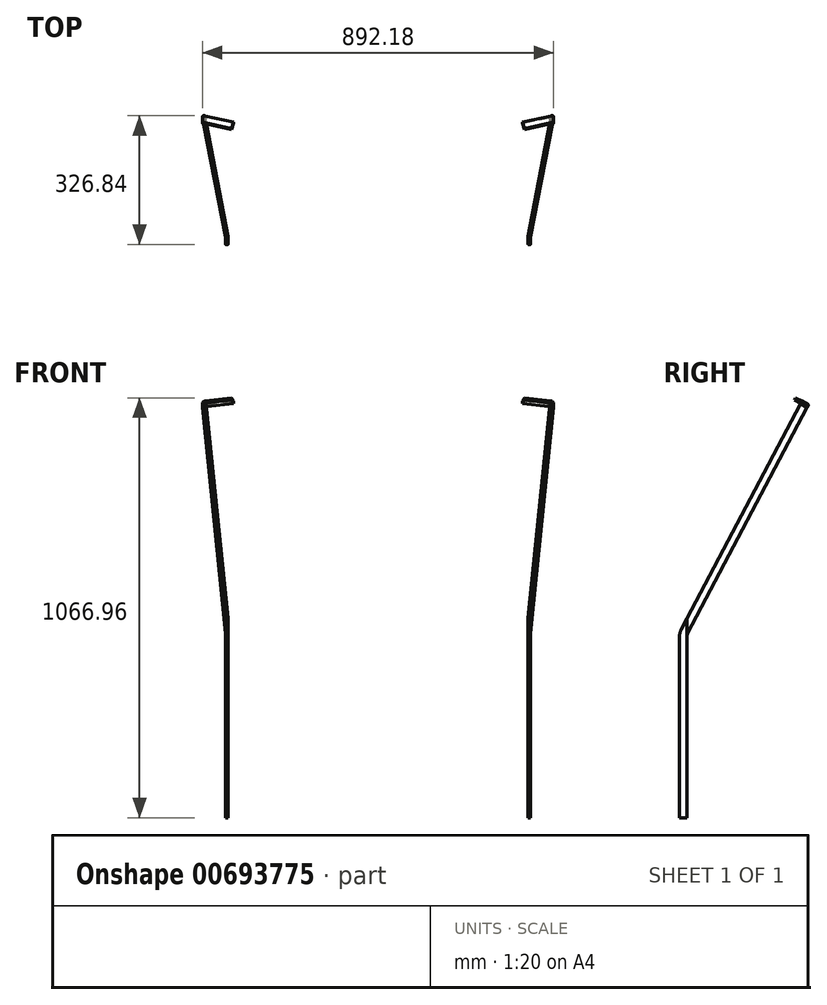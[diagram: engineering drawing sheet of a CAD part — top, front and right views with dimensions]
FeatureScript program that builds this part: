
annotation { "Feature Type Name" : "Feature", "Feature Type Description" : "" }
export const myFeature = defineFeature(function(context is Context, id is Id, definition is map)
    precondition{}
    {
        {
            var Q0;
            Q0=qCreatedBy(makeId("Right.planeOp"),FACE);
            var sketch = newSketch(context, id + "F0", { "sketchPlane" : qUnion([Q0])});
            skLineSegment(sketch, "E0.bottom", {"start": v(0, 0) * mm, "end": v(19.05, 0) * mm});
            skLineSegment(sketch, "E0.left", {"start": v(0, 0) * mm, "end": v(0, 462.04) * mm});
            skLineSegment(sketch, "E0.right", {"start": v(19.05, 0) * mm, "end": v(19.05, 462.04) * mm});
            skLineSegment(sketch, "E1", {"start": v(3.66, 476.85) * mm, "end": v(307.26, 1052.67) * mm});
            skLineSegment(sketch, "E2.0", {"start": v(20.52, 467.97) * mm, "end": v(323.77, 1043.14) * mm});
            skLineSegment(sketch, "E3", {"start": v(307.26, 1052.67) * mm, "end": v(323.77, 1043.14) * mm});
            skPoint(sketch, "E4.visualSharp", {"position": v(19.05, 465.19) * mm});
            skArc(sketch, "E4.filletArc", {"start": v(20.52, 467.97) * mm, "mid": v(19.42, 465.1) * mm, "end": v(19.05, 462.04) * mm});
            skArc(sketch, "E5", {"start": v(3.66, 476.85) * mm, "mid": v(0.93, 469.67) * mm, "end": v(0, 462.04) * mm});
            skPoint(sketch, "E6.orphan", {"position": v(0, 469.9) * mm});
            skLineSegment(sketch, "E7", {"start": v(9.53, 0) * mm, "end": v(9.53, 456.5) * mm, "construction": true});
            skLineSegment(sketch, "E8", {"start": v(315.52, 1047.9) * mm, "end": v(14.75, 477.45) * mm, "construction": true});
            skPoint(sketch, "E9", {"position": v(9.53, 57.15) * mm});
            skPoint(sketch, "E10", {"position": v(9.53, 101.6) * mm});
            skPoint(sketch, "E11", {"position": v(9.53, 127) * mm});
            skPoint(sketch, "E12", {"position": v(9.53, 203.2) * mm});
            skPoint(sketch, "E13", {"position": v(9.53, 355.6) * mm});
            skPoint(sketch, "E14", {"position": v(299.22, 1017) * mm});
            skPoint(sketch, "E15", {"position": v(271.8, 965) * mm});
            skPoint(sketch, "E16", {"position": v(238.46, 901.75) * mm});
            skPoint(sketch, "E17", {"position": v(179.93, 790.74) * mm});
            skPoint(sketch, "E18", {"position": v(149.55, 733.12) * mm});
            skPoint(sketch, "E19", {"position": v(120.65, 678.31) * mm});
            skPoint(sketch, "E20", {"position": v(61.38, 565.89) * mm});
            skPoint(sketch, "E21", {"position": v(29.52, 505.46) * mm});
            skPoint(sketch, "E22", {"position": v(29.73, 505.86) * mm});
            skSolve(sketch);
        }
        {
            var Q0;
            Q0 = qSketchRegion(id + "F0", true);
            extrude(context, id + "F1", {"entities" : qUnion([Q0]), "depth" : 76.2 * mm, "offsetDistance" : 25.4 * mm});
        }
        {
            var Q0;
            Q0=makeQuery(id+"F1.opExtrude","SWEPT_FACE",FACE,{"disambiguationData":[OSD([sQuery(id+"F0.wireOp",EDGE,"E0.left")])]});
            var sketch = newSketch(context, id + "F2", { "sketchPlane" : qUnion([Q0])});
            skLineSegment(sketch, "E23.bottom", {"start": v(6.35, 0) * mm, "end": v(76.2, 0) * mm});
            skLineSegment(sketch, "E23.top", {"start": v(6.35, 462.04) * mm, "end": v(76.2, 462.04) * mm});
            skLineSegment(sketch, "E23.left", {"start": v(6.35, 0) * mm, "end": v(6.35, 462.04) * mm});
            skLineSegment(sketch, "E23.right", {"start": v(76.2, 0) * mm, "end": v(76.2, 462.04) * mm});
            skSolve(sketch);
        }
        {
            var Q0;
            Q0=makeQuery(id+"F1.opExtrude","SWEPT_FACE",FACE,{"disambiguationData":[OSD([sQuery(id+"F0.wireOp",EDGE,"E1")])]});
            cPlane(context, id + "F3", {"entities" : qUnion([Q0]), "cplaneType" : CPlaneType.OFFSET, "offset" : 0 * mm, "width" : 152.4 * mm, "height" : 152.4 * mm});
        }
        {
            var Q0;
            Q0 = qSketchRegion(id + "F2", true);
            extrude(context, id + "F4", {"entities" : qUnion([Q0]), "operationType" : NewBodyOperationType.REMOVE, "endBound" : BoundingType.THROUGH_ALL, "oppositeDirection" : true, "depth" : 25.4 * mm, "offsetDistance" : 25.4 * mm});
        }
        {
            var Q0;
            Q0=qCreatedBy(makeId("Front.planeOp"),FACE);
            var sketch = newSketch(context, id + "F5", { "sketchPlane" : qUnion([Q0])});
            skPoint(sketch, "E24.0", {"position": v(6.35, 462.04) * mm});
            skLineSegment(sketch, "E25", {"start": v(6.9, 467.1) * mm, "end": v(66.3, 1052.67) * mm});
            skLineSegment(sketch, "E26", {"start": v(59.92, 1052.67) * mm, "end": v(0, 462.04) * mm});
            skLineSegment(sketch, "E27.0", {"start": v(66.3, 1052.67) * mm, "end": v(59.92, 1052.67) * mm});
            skPoint(sketch, "E28.orphan", {"position": v(0, 1052.67) * mm});
            skPoint(sketch, "E29.orphan", {"position": v(76.2, 1052.67) * mm});
            skLineSegment(sketch, "E30", {"start": v(0, 462.04) * mm, "end": v(0, 1052.67) * mm});
            skLineSegment(sketch, "E31", {"start": v(0, 1052.67) * mm, "end": v(59.92, 1052.67) * mm});
            skSolve(sketch);
        }
        {
            var Q0;
            Q0=qCreatedBy(makeId("Top.planeOp"),FACE);
            var Q1;
            Q1=sQuery(id+"F5.wireOp",VERTEX,"E28.orphan");
            cPlane(context, id + "F6", {"entities" : qUnion([Q0, Q1]), "cplaneType" : CPlaneType.PLANE_POINT, "offset" : 1059.18 * mm, "width" : 152.4 * mm, "height" : 152.4 * mm});
        }
        {
            var Q0;
            Q0=qCreatedBy(id+"F6.planeOp",FACE);
            var sketch = newSketch(context, id + "F7", { "sketchPlane" : qUnion([Q0])});
            skLineSegment(sketch, "E32.0", {"start": v(6.35, 0) * mm, "end": v(76.2, 0) * mm});
            skLineSegment(sketch, "E33", {"start": v(0, 3.66) * mm, "end": v(0, 19.05) * mm});
            skLineSegment(sketch, "E34.0", {"start": v(6.35, 0) * mm, "end": v(6.35, 19.05) * mm});
            skLineSegment(sketch, "E35", {"start": v(6.35, 19.05) * mm, "end": v(65.06, 323.77) * mm});
            skLineSegment(sketch, "E36.0", {"start": v(0.11, 20.25) * mm, "end": v(58.6, 323.77) * mm});
            skArc(sketch, "E37", {"start": v(0.11, 20.25) * mm, "mid": v(0.03, 19.65) * mm, "end": v(0, 19.05) * mm});
            skLineSegment(sketch, "E38", {"start": v(0.11, 20.25) * mm, "end": v(2.22, 31.18) * mm});
            skLineSegment(sketch, "E39.0", {"start": v(76.2, 323.77) * mm, "end": v(65.06, 323.77) * mm});
            skLineSegment(sketch, "E40.0", {"start": v(0, 307.26) * mm, "end": v(0, 323.77) * mm});
            skLineSegment(sketch, "E41.0", {"start": v(76.2, 307.26) * mm, "end": v(76.2, 323.77) * mm});
            skLineSegment(sketch, "E42.0", {"start": v(0, 19.05) * mm, "end": v(0, 307.26) * mm});
            skLineSegment(sketch, "E43.0", {"start": v(76.2, 0) * mm, "end": v(76.2, 307.26) * mm});
            skPoint(sketch, "E44.orphan", {"position": v(59.92, 0) * mm});
            skPoint(sketch, "E45.orphan", {"position": v(76.2, 3.66) * mm});
            skPoint(sketch, "E46.orphan", {"position": v(0, 3.66) * mm});
            skPoint(sketch, "E47.orphan", {"position": v(0, 0) * mm});
            skLineSegment(sketch, "E48.trimOffspring", {"start": v(58.6, 323.77) * mm, "end": v(0, 323.77) * mm});
            skSolve(sketch);
        }
        {
            var Q0;
            Q0=sQuery(id+"F7.wireOp",EDGE,"E35");
            cPlane(context, id + "F8", {"entities" : qUnion([Q0]), "cplaneType" : CPlaneType.LINE_ANGLE, "offset" : 25.4 * mm, "angle" : 90 * degree, "width" : 152.4 * mm, "height" : 152.4 * mm});
        }
        {
            var Q0;
            Q0=makeQuery(id+"F7.imprint","IMPRINT",FACE,{"disambiguationData":[TD([[makeQuery(id+"F7.imprint","IMPRINT",EDGE,{"derivedFrom":sQuery(id+"F7.wireOp",EDGE,"E36.0")}),1.0]])]});
            var Q1;
            Q1=makeQuery(id+"F7.imprint","IMPRINT",FACE,{"disambiguationData":[TD([[makeQuery(id+"F7.imprint","IMPRINT",EDGE,{"derivedFrom":sQuery(id+"F7.wireOp",EDGE,"E32.0")}),1.0]])]});
            extrude(context, id + "F9", {"entities" : qUnion([Q0, Q1]), "operationType" : NewBodyOperationType.REMOVE, "endBound" : BoundingType.THROUGH_ALL, "oppositeDirection" : true, "depth" : 25.4 * mm, "offsetDistance" : 25.4 * mm});
        }
        {
            var Q0;
            Q0=qCreatedBy(id+"F8.planeOp",FACE);
            var sketch = newSketch(context, id + "F10", { "sketchPlane" : qUnion([Q0])});
            skLineSegment(sketch, "E49.0", {"start": v(19.9, 506.03) * mm, "end": v(313.42, 1052.67) * mm});
            skLineSegment(sketch, "E50.0", {"start": v(21.4, 467.97) * mm, "end": v(330.23, 1043.14) * mm});
            skSolve(sketch);
        }
        {
            var Q0;
            Q0=qCreatedBy(id+"F3.planeOp",FACE);
            var sketch = newSketch(context, id + "F11", { "sketchPlane" : qUnion([Q0])});
            skPoint(sketch, "E51.0", {"position": v(55.42, 1074.48) * mm});
            skLineSegment(sketch, "E52", {"start": v(-51.16, 1074.73) * mm, "end": v(-51.16, 1081.08) * mm});
            skLineSegment(sketch, "E53", {"start": v(-51.16, 1081.08) * mm, "end": v(58.57, 1080.82) * mm});
            skLineSegment(sketch, "E54.0", {"start": v(53.7, 1074.48) * mm, "end": v(-51.16, 1074.73) * mm});
            skArc(sketch, "E55.filletArc", {"start": v(55.28, 1073.02) * mm, "mid": v(54.78, 1074.06) * mm, "end": v(53.7, 1074.48) * mm});
            skPoint(sketch, "E56.orphan", {"position": v(61.88, 1074.48) * mm});
            skPoint(sketch, "E57.0.start.orphan", {"position": v(6.35, 456.51) * mm});
            skPoint(sketch, "E58.0.start.orphan", {"position": v(0.11, 459.09) * mm});
            skLineSegment(sketch, "E59.0", {"start": v(65, 1073) * mm, "end": v(65.06, 1073.75) * mm});
            skLineSegment(sketch, "E60.0.0", {"start": v(6.35, 423.52) * mm, "end": v(6.35, 456.51) * mm});
            skEllipticalArc(sketch, "E60.0.4", {});
            skLineSegment(sketch, "E60.0.5", {"start": v(0, 456.51) * mm, "end": v(0, 423.52) * mm});
            skLineSegment(sketch, "E60.0.6", {"start": v(0, 423.52) * mm, "end": v(6.35, 423.52) * mm});
            skLineSegment(sketch, "E61", {"start": v(55.28, 1073.02) * mm, "end": v(65, 1073) * mm});
            skArc(sketch, "E62", {"start": v(65.06, 1073.75) * mm, "mid": v(63.37, 1078.7) * mm, "end": v(58.57, 1080.82) * mm});
            skPoint(sketch, "E63.orphan", {"position": v(6.63, 423.52) * mm});
            const initialGuessF11  = {"E60.0.4": [0.00635, 0.45651053869236363, 0, 1, 0.013615310578773647, 0.00634999895801842, 1.3804491440357622, 1.5707963267948966]};
            skSetInitialGuess(sketch, initialGuessF11);
            skSolve(sketch);
        }
        {
            var Q0;
            Q0=makeQuery(id+"F11.imprint","IMPRINT",FACE,{"disambiguationData":[TD([[makeQuery(id+"F11.imprint","IMPRINT",EDGE,{"derivedFrom":sQuery(id+"F11.wireOp",EDGE,"E52")}),-1.0]])]});
            extrude(context, id + "F12", {"entities" : qUnion([Q0]), "operationType" : NewBodyOperationType.ADD, "endBound" : BoundingType.SYMMETRIC, "depth" : 76.2 * mm, "offsetDistance" : 25.4 * mm});
        }
        {
            var Q0;
            Q0=makeQuery(id+"F12.opExtrude","SWEPT_FACE",FACE,{"disambiguationData":[OSD([sQuery(id+"F11.wireOp",EDGE,"E53")])]});
            var sketch = newSketch(context, id + "F13", { "sketchPlane" : qUnion([Q0])});
            skLineSegment(sketch, "E64.0", {"start": v(60.17, -199.7) * mm, "end": v(57.2, -217.64) * mm});
            skLineSegment(sketch, "E65", {"start": v(63.46, -199.36) * mm, "end": v(61.5, -199.36) * mm});
            skLineSegment(sketch, "E66", {"start": v(63.44, -218.52) * mm, "end": v(-11.78, -237.46) * mm});
            skLineSegment(sketch, "E67.0", {"start": v(61.5, -199.36) * mm, "end": v(-16.43, -218.99) * mm});
            skLineSegment(sketch, "E68", {"start": v(-16.43, -218.99) * mm, "end": v(-11.78, -237.46) * mm});
            skPoint(sketch, "E69.orphan", {"position": v(60.22, -199.36) * mm});
            skLineSegment(sketch, "E70.0", {"start": v(-53.7, -257.26) * mm, "end": v(-53.7, -257.26) * mm});
            skLineSegment(sketch, "E71", {"start": v(63.46, -181.06) * mm, "end": v(63.46, -199.36) * mm});
            skLineSegment(sketch, "E72.0", {"start": v(63.46, -181.06) * mm, "end": v(50.64, -181.06) * mm});
            skLineSegment(sketch, "E73.0", {"start": v(-53.7, -181.06) * mm, "end": v(50.64, -181.06) * mm});
            skLineSegment(sketch, "E74.0", {"start": v(-53.7, -257.26) * mm, "end": v(-53.7, -181.06) * mm});
            skLineSegment(sketch, "E75.0", {"start": v(63.44, -257.26) * mm, "end": v(-53.7, -257.26) * mm});
            skLineSegment(sketch, "E76.0", {"start": v(63.44, -257.26) * mm, "end": v(63.44, -218.52) * mm});
            skLineSegment(sketch, "E77.trimOffspring", {"start": v(63.44, -199.36) * mm, "end": v(63.44, -181.06) * mm});
            skSolve(sketch);
        }
        {
            var Q0;
            Q0 = qSketchRegion(id + "F13", true);
            extrude(context, id + "F14", {"entities" : qUnion([Q0]), "operationType" : NewBodyOperationType.REMOVE, "oppositeDirection" : true, "depth" : 7.94 * mm, "offsetDistance" : 25.4 * mm});
        }
        {
            var Q0;
            Q0=qCreatedBy(makeId("Right.planeOp"),FACE);
            cPlane(context, id + "F15", {"entities" : qUnion([Q0]), "cplaneType" : CPlaneType.OFFSET, "offset" : 381 * mm, "oppositeDirection" : true, "width" : 152.4 * mm, "height" : 152.4 * mm});
        }
        {
            var Q0;
            Q0=makeQuery(id+"F1.opExtrude","SWEPT_BODY",BODY,{"disambiguationData":[OSD([sQuery(id+"F0.wireOp",EDGE,"E0.bottom"),sQuery(id+"F0.wireOp",EDGE,"E0.left"),sQuery(id+"F0.wireOp",EDGE,"E0.right"),sQuery(id+"F0.wireOp",EDGE,"E1"),sQuery(id+"F0.wireOp",EDGE,"E2.0"),sQuery(id+"F0.wireOp",EDGE,"E3"),sQuery(id+"F0.wireOp",EDGE,"E4.filletArc"),sQuery(id+"F0.wireOp",EDGE,"E5")])]});
            var Q1;
            Q1=qCreatedBy(id+"F15.planeOp",FACE);
            mirror(context, id + "F16", {"entities" : qUnion([Q0]), "mirrorPlane" : qUnion([Q1])});
        }
    });
